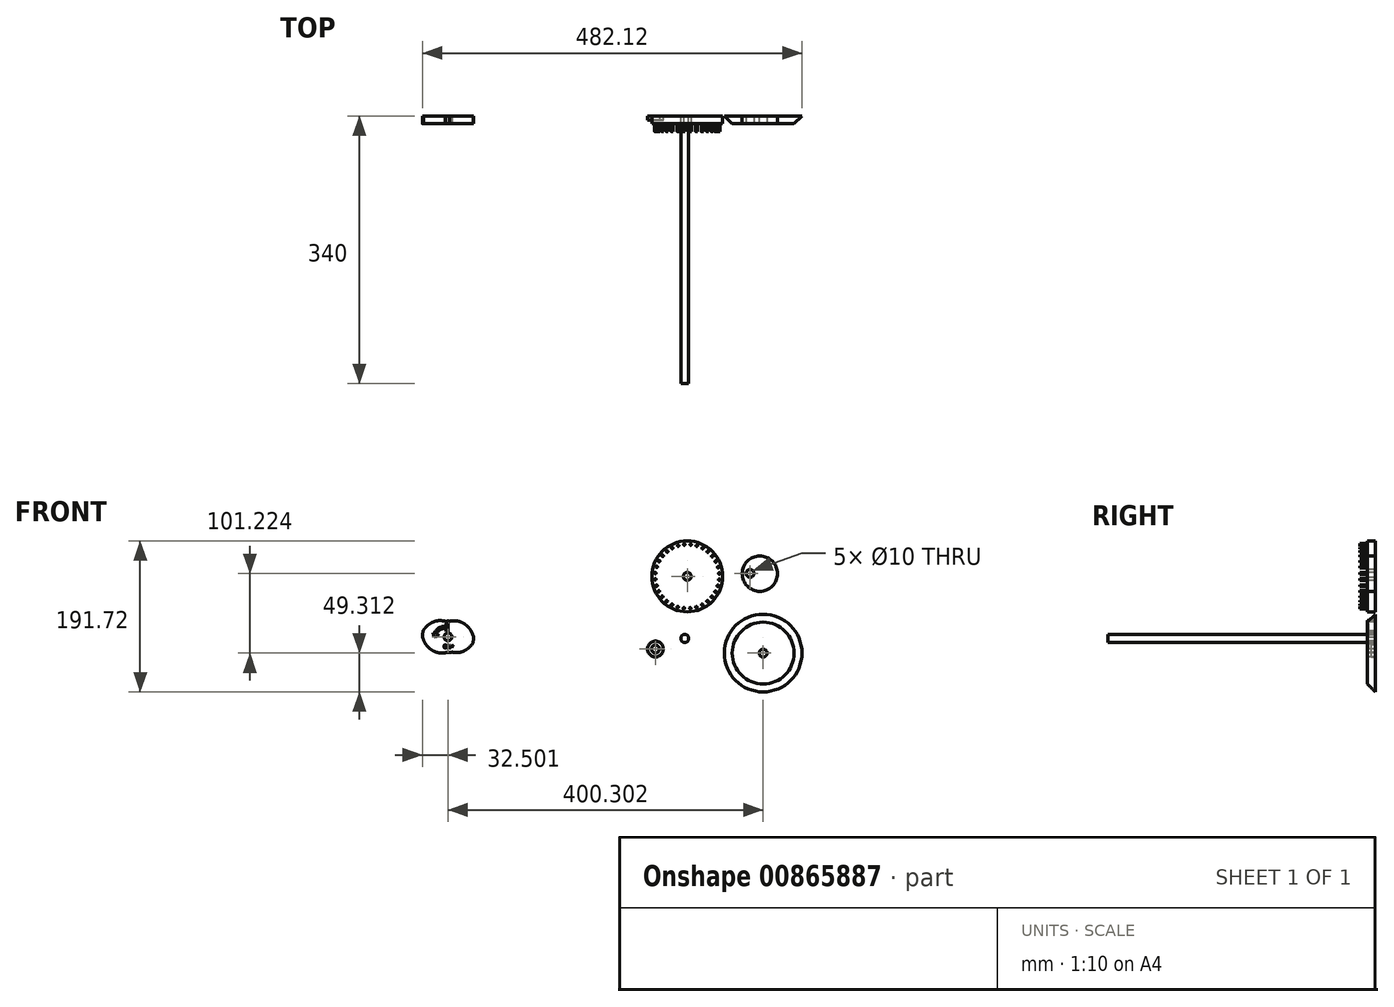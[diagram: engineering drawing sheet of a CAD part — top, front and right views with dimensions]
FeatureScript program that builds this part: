
annotation { "Feature Type Name" : "Feature", "Feature Type Description" : "" }
export const myFeature = defineFeature(function(context is Context, id is Id, definition is map)
    precondition{}
    {
        {
            var Q0;
            Q0=qCreatedBy(makeId("Front.planeOp"),FACE);
            var sketch = newSketch(context, id + "F0", { "sketchPlane" : qUnion([Q0])});
            skCircle(sketch, "E0", {"center": v(-46.7, 45.56) * mm, "radius": 45 * mm});
            skCircle(sketch, "E1", {"center": v(45.46, 49.07) * mm, "radius": 22.45 * mm});
            skCircle(sketch, "E2", {"center": v(49.66, -51.85) * mm, "radius": 49.31 * mm});
            skCircle(sketch, "E3", {"center": v(-350.64, -31.3) * mm, "radius": 20 * mm});
            skArc(sketch, "E4", {"start": v(-382.03, -22.88) * mm, "mid": v(-382.86, -27.05) * mm, "end": v(-383.14, -31.3) * mm});
            skLineSegment(sketch, "E5", {"start": v(-350.64, -11.3) * mm, "end": v(-350.64, 1.2) * mm});
            skLineSegment(sketch, "E6.1.0", {"start": v(-355.82, -11.98) * mm, "end": v(-359.05, 0.1) * mm});
            skLineSegment(sketch, "E6.2.0", {"start": v(-360.64, -13.97) * mm, "end": v(-366.89, -3.15) * mm});
            skLineSegment(sketch, "E6.3.0", {"start": v(-364.78, -17.15) * mm, "end": v(-373.62, -8.31) * mm});
            skLineSegment(sketch, "E6.4.0", {"start": v(-367.96, -21.3) * mm, "end": v(-378.79, -15.04) * mm});
            skLineSegment(sketch, "E6.5.0", {"start": v(-369.96, -26.12) * mm, "end": v(-382.03, -22.88) * mm});
            skLineSegment(sketch, "E6.6.0", {"start": v(-370.64, -31.3) * mm, "end": v(-383.14, -31.3) * mm});
            skLineSegment(sketch, "E6.7.0", {"start": v(-369.96, -36.47) * mm, "end": v(-382.03, -39.7) * mm});
            skLineSegment(sketch, "E6.8.0", {"start": v(-367.96, -41.3) * mm, "end": v(-378.79, -47.54) * mm});
            skLineSegment(sketch, "E6.9.0", {"start": v(-364.78, -45.44) * mm, "end": v(-373.62, -54.27) * mm});
            skLineSegment(sketch, "E6.10.0", {"start": v(-360.64, -48.61) * mm, "end": v(-366.89, -59.44) * mm});
            skLineSegment(sketch, "E6.11.0", {"start": v(-355.82, -50.61) * mm, "end": v(-359.05, -62.69) * mm});
            skLineSegment(sketch, "E6.12.0", {"start": v(-350.64, -51.3) * mm, "end": v(-350.64, -63.8) * mm});
            skLineSegment(sketch, "E6.13.0", {"start": v(-345.46, -50.61) * mm, "end": v(-342.23, -62.69) * mm});
            skLineSegment(sketch, "E6.14.0", {"start": v(-340.64, -48.61) * mm, "end": v(-334.39, -59.44) * mm});
            skLineSegment(sketch, "E6.15.0", {"start": v(-336.5, -45.44) * mm, "end": v(-327.66, -54.27) * mm});
            skLineSegment(sketch, "E6.16.0", {"start": v(-333.32, -41.3) * mm, "end": v(-322.5, -47.54) * mm});
            skLineSegment(sketch, "E6.17.0", {"start": v(-331.32, -36.47) * mm, "end": v(-319.25, -39.7) * mm});
            skLineSegment(sketch, "E6.18.0", {"start": v(-330.64, -31.3) * mm, "end": v(-318.14, -31.3) * mm});
            skLineSegment(sketch, "E6.19.0", {"start": v(-331.32, -26.12) * mm, "end": v(-319.25, -22.88) * mm});
            skLineSegment(sketch, "E6.20.0", {"start": v(-333.32, -21.3) * mm, "end": v(-322.5, -15.04) * mm});
            skLineSegment(sketch, "E6.21.0", {"start": v(-336.5, -17.15) * mm, "end": v(-327.66, -8.31) * mm});
            skLineSegment(sketch, "E6.22.0", {"start": v(-340.64, -13.97) * mm, "end": v(-334.39, -3.15) * mm});
            skLineSegment(sketch, "E6.23.0", {"start": v(-345.46, -11.98) * mm, "end": v(-342.23, 0.1) * mm});
            skPoint(sketch, "E7", {"position": v(-382.03, -22.88) * mm});
            skPoint(sketch, "E8", {"position": v(-383.14, -31.3) * mm});
            skPoint(sketch, "E9", {"position": v(-318.14, -31.3) * mm});
            skPoint(sketch, "E10", {"position": v(-319.25, -39.7) * mm});
            skPoint(sketch, "E11", {"position": v(-353.64, -11.52) * mm});
            skPoint(sketch, "E12", {"position": v(-345.46, -50.61) * mm});
            skPoint(sketch, "E13", {"position": v(-352.64, -51.2) * mm});
            skLineSegment(sketch, "E14", {"start": v(-350.64, -31.3) * mm, "end": v(-345.46, -50.61) * mm, "construction": true});
            skLineSegment(sketch, "E15", {"start": v(-350.64, -31.3) * mm, "end": v(-352.64, -51.2) * mm, "construction": true});
            skLineSegment(sketch, "E16", {"start": v(-350.64, -31.3) * mm, "end": v(-353.64, -11.52) * mm, "construction": true});
            skLineSegment(sketch, "E17", {"start": v(-350.64, -31.3) * mm, "end": v(-348.64, -11.4) * mm, "construction": true});
            skPoint(sketch, "E18", {"position": v(-348.64, -11.4) * mm});
            skPoint(sketch, "E19", {"position": v(-345.2, -11) * mm});
            skPoint(sketch, "E20", {"position": v(-338.99, -11.12) * mm});
            skPoint(sketch, "E21", {"position": v(-332.54, -13.2) * mm});
            skPoint(sketch, "E22", {"position": v(-326.48, -17.34) * mm});
            skPoint(sketch, "E23", {"position": v(-321.47, -23.48) * mm});
            skPoint(sketch, "E24", {"position": v(-325.2, -45.98) * mm});
            skPoint(sketch, "E25", {"position": v(-332.08, -49.86) * mm});
            skPoint(sketch, "E26", {"position": v(-339.08, -51.32) * mm});
            skPoint(sketch, "E27", {"position": v(-356.07, -51.58) * mm});
            skPoint(sketch, "E28", {"position": v(-362.29, -51.47) * mm});
            skPoint(sketch, "E29", {"position": v(-368.74, -49.4) * mm});
            skPoint(sketch, "E30", {"position": v(-374.8, -45.24) * mm});
            skPoint(sketch, "E31", {"position": v(-379.81, -39.11) * mm});
            skPoint(sketch, "E32", {"position": v(-376.3, -16.48) * mm});
            skPoint(sketch, "E33", {"position": v(-369.55, -12.38) * mm});
            skPoint(sketch, "E34", {"position": v(-362.57, -10.62) * mm});
            skPoint(sketch, "E35", {"position": v(-356.07, -11) * mm});
            skFitSpline(sketch, "E36", {"points": [v(-382.03, -22.88) * mm, v(-376.3, -16.48) * mm, v(-369.55, -12.38) * mm, v(-362.57, -10.62) * mm, v(-356.07, -11) * mm, v(-353.64, -11.52) * mm], "startDerivative": vector(23.19, 29.3) * mm, "endDerivative": vector(16.8, -4.09) * mm});
            skFitSpline(sketch, "E37", {"points": [v(-348.64, -11.4) * mm, v(-345.2, -11) * mm, v(-338.99, -11.12) * mm, v(-332.54, -13.2) * mm, v(-326.48, -17.34) * mm, v(-321.47, -23.48) * mm, v(-318.14, -31.3) * mm], "startDerivative": vector(26.16, 3.52) * mm, "endDerivative": vector(15.37, -42.82) * mm});
            skFitSpline(sketch, "E38", {"points": [v(-319.25, -39.7) * mm, v(-325.2, -45.98) * mm, v(-332.08, -49.86) * mm, v(-339.08, -51.32) * mm, v(-345.46, -50.61) * mm], "startDerivative": vector(-21.1, -25.12) * mm, "endDerivative": vector(-27.27, 4.92) * mm});
            skFitSpline(sketch, "E39", {"points": [v(-352.64, -51.2) * mm, v(-356.07, -51.58) * mm, v(-362.29, -51.47) * mm, v(-368.74, -49.4) * mm, v(-374.8, -45.24) * mm, v(-379.81, -39.11) * mm, v(-383.14, -31.3) * mm], "startDerivative": vector(-26.17, -3.52) * mm, "endDerivative": vector(-15.37, 42.82) * mm});
            skArc(sketch, "E40.trimOffspring", {"start": v(-319.25, -39.7) * mm, "mid": v(-318.42, -35.54) * mm, "end": v(-318.14, -31.3) * mm});
            skSolve(sketch);
        }
        {
            var Q0;
            Q0=qSketchRegion(id+"F0",true);
            extrude(context, id + "F1", {"entities" : qUnion([Q0]), "depth" : 10 * mm, "offsetDistance" : 25 * mm});
        }
        {
            var Q0;
            Q0=makeQuery(id+"F1.opExtrude","CAP_FACE",FACE,{"disambiguationData":[OSD([sQuery(id+"F0.wireOp",EDGE,"E0")])],"isStart":false});
            var sketch = newSketch(context, id + "F2", { "sketchPlane" : qUnion([Q0])});
            skCircle(sketch, "E41", {"center": v(-46.7, 45.56) * mm, "radius": 5 * mm});
            skSolve(sketch);
        }
        {
            var Q0;
            Q0=qSketchRegion(id+"F2",true);
            extrude(context, id + "F3", {"entities" : qUnion([Q0]), "operationType" : NewBodyOperationType.REMOVE, "endBound" : BoundingType.THROUGH_ALL, "oppositeDirection" : true, "depth" : 25 * mm, "offsetDistance" : 25 * mm});
        }
        {
            var Q0;
            Q0=makeQuery(id+"F1.opExtrude","CAP_FACE",FACE,{"disambiguationData":[OSD([sQuery(id+"F0.wireOp",EDGE,"E2")])],"isStart":false});
            var sketch = newSketch(context, id + "F4", { "sketchPlane" : qUnion([Q0])});
            skCircle(sketch, "E42", {"center": v(49.66, -51.85) * mm, "radius": 5 * mm});
            skSolve(sketch);
        }
        {
            var Q0;
            Q0=qSketchRegion(id+"F4",true);
            extrude(context, id + "F5", {"entities" : qUnion([Q0]), "operationType" : NewBodyOperationType.REMOVE, "endBound" : BoundingType.THROUGH_ALL, "oppositeDirection" : true, "depth" : 25 * mm, "offsetDistance" : 25 * mm});
        }
        {
            var Q0;
            Q0=makeQuery(id+"F1.opExtrude","CAP_FACE",FACE,{"disambiguationData":[OSD([sQuery(id+"F0.wireOp",EDGE,"E1")])],"isStart":false});
            var sketch = newSketch(context, id + "F6", { "sketchPlane" : qUnion([Q0])});
            skCircle(sketch, "E43", {"center": v(33.01, 49.38) * mm, "radius": 5 * mm});
            skSolve(sketch);
        }
        {
            var Q0;
            Q0=qSketchRegion(id+"F6",true);
            extrude(context, id + "F7", {"entities" : qUnion([Q0]), "operationType" : NewBodyOperationType.REMOVE, "endBound" : BoundingType.THROUGH_ALL, "oppositeDirection" : true, "depth" : 25 * mm, "offsetDistance" : 25 * mm});
        }
        {
            var Q0;
            Q0=makeQuery(id+"F1.opExtrude","CAP_EDGE",EDGE,{"disambiguationData":[OSD([sQuery(id+"F0.wireOp",EDGE,"E2")])],"isStart":false});
            chamfer(context, id + "F8", {"entities" : qUnion([Q0]), "width" : 10 * mm, "tangentPropagation" : true});
        }
        {
            var Q0;
            Q0=qCreatedBy(makeId("Front.planeOp"),FACE);
            var sketch = newSketch(context, id + "F9", { "sketchPlane" : qUnion([Q0])});
            skCircle(sketch, "E44", {"center": v(-49.88, -33.26) * mm, "radius": 5 * mm});
            skSolve(sketch);
        }
        {
            var Q0;
            Q0=qSketchRegion(id+"F9",true);
            extrude(context, id + "F10", {"entities" : qUnion([Q0]), "depth" : 340 * mm, "offsetDistance" : 25 * mm});
        }
        {
            var Q0;
            Q0=qCreatedBy(makeId("Front.planeOp"),FACE);
            var sketch = newSketch(context, id + "F11", { "sketchPlane" : qUnion([Q0])});
            skCircle(sketch, "E45", {"center": v(-87.17, -46.68) * mm, "radius": 10 * mm});
            skSolve(sketch);
        }
        {
            var Q0;
            Q0=qSketchRegion(id+"F11",true);
            extrude(context, id + "F12", {"entities" : qUnion([Q0]), "depth" : 5 * mm, "offsetDistance" : 25 * mm});
        }
        {
            var Q0;
            Q0=makeQuery(id+"F12.opExtrude","CAP_FACE",FACE,{"disambiguationData":[OSD([sQuery(id+"F11.wireOp",EDGE,"E45")])],"isStart":false});
            var sketch = newSketch(context, id + "F13", { "sketchPlane" : qUnion([Q0])});
            skCircle(sketch, "E46", {"center": v(-87.17, -46.68) * mm, "radius": 5 * mm});
            skSolve(sketch);
        }
        {
            var Q0;
            Q0=qSketchRegion(id+"F13",true);
            extrude(context, id + "F14", {"entities" : qUnion([Q0]), "operationType" : NewBodyOperationType.REMOVE, "endBound" : BoundingType.THROUGH_ALL, "oppositeDirection" : true, "depth" : 25 * mm, "offsetDistance" : 25 * mm});
        }
        {
            var Q0;
            Q0=makeQuery(id+"F1.opExtrude","CAP_FACE",FACE,{"disambiguationData":[OSD([sQuery(id+"F0.wireOp",EDGE,"E0")])],"isStart":false});
            var sketch = newSketch(context, id + "F15", { "sketchPlane" : qUnion([Q0])});
            skArc(sketch, "E47.cCircle", {"start": v(-41.46, 85.98) * mm, "mid": v(-54.9, 5.65) * mm, "end": v(-35.59, 84.77) * mm, "construction": true});
            skLineSegment(sketch, "E47.0", {"start": v(-21.04, 13.9) * mm, "end": v(-27.7, 9.5) * mm});
            skLineSegment(sketch, "E47.1", {"start": v(-27.7, 9.5) * mm, "end": v(-35.1, 6.5) * mm});
            skLineSegment(sketch, "E47.2", {"start": v(-35.1, 6.5) * mm, "end": v(-42.95, 4.99) * mm});
            skLineSegment(sketch, "E47.3", {"start": v(-42.95, 4.99) * mm, "end": v(-50.94, 5.03) * mm});
            skLineSegment(sketch, "E47.4", {"start": v(-50.94, 5.03) * mm, "end": v(-58.76, 6.64) * mm});
            skLineSegment(sketch, "E47.5", {"start": v(-58.76, 6.64) * mm, "end": v(-66.13, 9.74) * mm});
            skLineSegment(sketch, "E47.6", {"start": v(-66.13, 9.74) * mm, "end": v(-72.74, 14.22) * mm});
            skLineSegment(sketch, "E47.7", {"start": v(-72.74, 14.22) * mm, "end": v(-78.35, 19.9) * mm});
            skLineSegment(sketch, "E47.8", {"start": v(-78.35, 19.9) * mm, "end": v(-82.75, 26.57) * mm});
            skLineSegment(sketch, "E47.9", {"start": v(-82.75, 26.57) * mm, "end": v(-85.76, 33.97) * mm});
            skLineSegment(sketch, "E47.10", {"start": v(-85.76, 33.97) * mm, "end": v(-87.27, 41.82) * mm});
            skLineSegment(sketch, "E47.11", {"start": v(-87.27, 41.82) * mm, "end": v(-87.23, 49.8) * mm});
            skLineSegment(sketch, "E47.12", {"start": v(-87.23, 49.8) * mm, "end": v(-85.62, 57.63) * mm});
            skLineSegment(sketch, "E47.13", {"start": v(-85.62, 57.63) * mm, "end": v(-82.52, 65) * mm});
            skLineSegment(sketch, "E47.14", {"start": v(-82.52, 65) * mm, "end": v(-78.04, 71.6) * mm});
            skLineSegment(sketch, "E47.15", {"start": v(-78.04, 71.6) * mm, "end": v(-72.36, 77.22) * mm});
            skLineSegment(sketch, "E47.16", {"start": v(-72.36, 77.22) * mm, "end": v(-65.69, 81.62) * mm});
            skLineSegment(sketch, "E47.17", {"start": v(-65.69, 81.62) * mm, "end": v(-58.29, 84.63) * mm});
            skLineSegment(sketch, "E47.18", {"start": v(-58.29, 84.63) * mm, "end": v(-50.44, 86.14) * mm});
            skLineSegment(sketch, "E47.19", {"start": v(-50.44, 86.14) * mm, "end": v(-42.46, 86.1) * mm});
            skLineSegment(sketch, "E47.20", {"start": v(-42.46, 86.1) * mm, "end": v(-41.48, 85.9) * mm});
            skLineSegment(sketch, "E47.21", {"start": v(-34.63, 84.49) * mm, "end": v(-27.27, 81.38) * mm});
            skLineSegment(sketch, "E47.22", {"start": v(-27.27, 81.38) * mm, "end": v(-20.65, 76.9) * mm});
            skLineSegment(sketch, "E47.23", {"start": v(-20.65, 76.9) * mm, "end": v(-15.04, 71.22) * mm});
            skLineSegment(sketch, "E47.24", {"start": v(-15.04, 71.22) * mm, "end": v(-10.64, 64.55) * mm});
            skLineSegment(sketch, "E47.25", {"start": v(-10.64, 64.55) * mm, "end": v(-7.63, 57.15) * mm});
            skLineSegment(sketch, "E47.26", {"start": v(-7.63, 57.15) * mm, "end": v(-6.12, 49.31) * mm});
            skLineSegment(sketch, "E47.27", {"start": v(-6.12, 49.31) * mm, "end": v(-6.17, 41.32) * mm});
            skLineSegment(sketch, "E47.28", {"start": v(-6.17, 41.32) * mm, "end": v(-7.77, 33.5) * mm});
            skLineSegment(sketch, "E47.29", {"start": v(-7.77, 33.5) * mm, "end": v(-10.88, 26.14) * mm});
            skLineSegment(sketch, "E47.30", {"start": v(-10.88, 26.14) * mm, "end": v(-15.36, 19.52) * mm});
            skLineSegment(sketch, "E47.31", {"start": v(-15.36, 19.52) * mm, "end": v(-21.04, 13.9) * mm});
            skCircle(sketch, "E48", {"center": v(-15.04, 71.22) * mm, "radius": 1 * mm});
            skCircle(sketch, "E49", {"center": v(-10.64, 64.55) * mm, "radius": 1 * mm});
            skCircle(sketch, "E50", {"center": v(-7.63, 57.15) * mm, "radius": 1 * mm});
            skCircle(sketch, "E51", {"center": v(-6.12, 49.31) * mm, "radius": 1 * mm});
            skCircle(sketch, "E52", {"center": v(-6.17, 41.32) * mm, "radius": 1 * mm});
            skCircle(sketch, "E53", {"center": v(-7.77, 33.5) * mm, "radius": 1 * mm});
            skCircle(sketch, "E54", {"center": v(-10.88, 26.14) * mm, "radius": 1 * mm});
            skCircle(sketch, "E55", {"center": v(-15.36, 19.52) * mm, "radius": 1 * mm});
            skCircle(sketch, "E56", {"center": v(-21.04, 13.9) * mm, "radius": 1 * mm});
            skCircle(sketch, "E57", {"center": v(-27.7, 9.5) * mm, "radius": 1 * mm});
            skCircle(sketch, "E58", {"center": v(-35.1, 6.5) * mm, "radius": 1 * mm});
            skCircle(sketch, "E59", {"center": v(-42.95, 4.99) * mm, "radius": 1 * mm});
            skCircle(sketch, "E60", {"center": v(-50.94, 5.03) * mm, "radius": 1 * mm});
            skCircle(sketch, "E61", {"center": v(-58.76, 6.64) * mm, "radius": 1 * mm});
            skCircle(sketch, "E62", {"center": v(-66.13, 9.74) * mm, "radius": 1 * mm});
            skCircle(sketch, "E63", {"center": v(-72.74, 14.22) * mm, "radius": 1 * mm});
            skCircle(sketch, "E64", {"center": v(-78.35, 19.9) * mm, "radius": 1 * mm});
            skCircle(sketch, "E65", {"center": v(-87.27, 41.82) * mm, "radius": 1 * mm});
            skCircle(sketch, "E66", {"center": v(-85.76, 33.97) * mm, "radius": 1 * mm});
            skCircle(sketch, "E67", {"center": v(-82.75, 26.57) * mm, "radius": 1 * mm});
            skCircle(sketch, "E68", {"center": v(-87.23, 49.8) * mm, "radius": 1 * mm});
            skCircle(sketch, "E69", {"center": v(-85.62, 57.63) * mm, "radius": 1 * mm});
            skCircle(sketch, "E70", {"center": v(-82.52, 65) * mm, "radius": 1 * mm});
            skCircle(sketch, "E71", {"center": v(-78.04, 71.6) * mm, "radius": 1 * mm});
            skCircle(sketch, "E72", {"center": v(-72.36, 77.22) * mm, "radius": 1 * mm});
            skCircle(sketch, "E73", {"center": v(-65.69, 81.62) * mm, "radius": 1 * mm});
            skCircle(sketch, "E74", {"center": v(-58.29, 84.63) * mm, "radius": 1 * mm});
            skCircle(sketch, "E75", {"center": v(-50.44, 86.14) * mm, "radius": 1 * mm});
            skCircle(sketch, "E76", {"center": v(-42.46, 86.1) * mm, "radius": 1 * mm});
            skCircle(sketch, "E77", {"center": v(-34.63, 84.49) * mm, "radius": 1 * mm});
            skCircle(sketch, "E78", {"center": v(-27.27, 81.38) * mm, "radius": 1 * mm});
            skCircle(sketch, "E79", {"center": v(-20.65, 76.9) * mm, "radius": 1 * mm});
            skLineSegment(sketch, "E80.trimOffspring", {"start": v(-35.61, 84.69) * mm, "end": v(-34.63, 84.49) * mm});
            skSolve(sketch);
        }
        {
            var Q0;
            Q0=qSketchRegion(id+"F15",true);
            extrude(context, id + "F16", {"entities" : qUnion([Q0]), "operationType" : NewBodyOperationType.ADD, "depth" : 10 * mm, "offsetDistance" : 25 * mm});
        }
        {
            var Q0;
            Q0=makeQuery(id+"F1.opExtrude","CAP_FACE",FACE,{"disambiguationData":[OSD([sQuery(id+"F0.wireOp",EDGE,"E3"),sQuery(id+"F0.wireOp",EDGE,"E4"),sQuery(id+"F0.wireOp",EDGE,"E36"),sQuery(id+"F0.wireOp",EDGE,"E37"),sQuery(id+"F0.wireOp",EDGE,"E38"),sQuery(id+"F0.wireOp",EDGE,"E39"),sQuery(id+"F0.wireOp",EDGE,"E40.trimOffspring")])],"isStart":false});
            var sketch = newSketch(context, id + "F17", { "sketchPlane" : qUnion([Q0])});
            skCircle(sketch, "E81", {"center": v(-350.64, -31.3) * mm, "radius": 5 * mm});
            skSolve(sketch);
        }
        {
            var Q0;
            Q0 = qSketchRegion(id + "F17", true);
            extrude(context, id + "F18", {"entities" : qUnion([Q0]), "operationType" : NewBodyOperationType.REMOVE, "oppositeDirection" : true, "depth" : 25 * mm, "offsetDistance" : 25 * mm});
        }
        {
            var Q0;
            Q0=makeQuery(id+"F1.opExtrude","CAP_FACE",FACE,{"disambiguationData":[OSD([sQuery(id+"F0.wireOp",EDGE,"E3"),sQuery(id+"F0.wireOp",EDGE,"E4"),sQuery(id+"F0.wireOp",EDGE,"E36"),sQuery(id+"F0.wireOp",EDGE,"E37"),sQuery(id+"F0.wireOp",EDGE,"E38"),sQuery(id+"F0.wireOp",EDGE,"E39"),sQuery(id+"F0.wireOp",EDGE,"E40.trimOffspring")])],"isStart":false});
            var sketch = newSketch(context, id + "F19", { "sketchPlane" : qUnion([Q0])});
            skLineSegment(sketch, "E82", {"start": v(-350.7, -14.28) * mm, "end": v(-350.7, -24.2) * mm});
            skLineSegment(sketch, "E83", {"start": v(-350.7, -24.2) * mm, "end": v(-352.94, -24.2) * mm});
            skLineSegment(sketch, "E84", {"start": v(-352.94, -24.2) * mm, "end": v(-352.94, -20.48) * mm});
            skArc(sketch, "E85", {"start": v(-352.94, -20.48) * mm, "mid": v(-360.46, -22.08) * mm, "end": v(-365.35, -28) * mm});
            skLineSegment(sketch, "E86", {"start": v(-350.7, -14.28) * mm, "end": v(-353.02, -14.28) * mm});
            skLineSegment(sketch, "E87", {"start": v(-353.02, -14.28) * mm, "end": v(-353.02, -17.92) * mm});
            skArc(sketch, "E88", {"start": v(-353.02, -17.92) * mm, "mid": v(-361.68, -19.58) * mm, "end": v(-367.42, -26.27) * mm});
            skLineSegment(sketch, "E89", {"start": v(-367.42, -26.27) * mm, "end": v(-369.65, -25.36) * mm});
            skLineSegment(sketch, "E90", {"start": v(-369.65, -25.36) * mm, "end": v(-368.4, -31.32) * mm});
            skLineSegment(sketch, "E91", {"start": v(-368.4, -31.32) * mm, "end": v(-361.95, -29.97) * mm});
            skLineSegment(sketch, "E92", {"start": v(-361.95, -29.97) * mm, "end": v(-365.35, -28) * mm});
            skText(sketch, "E93", { "text": "Cour", "fontName": "OpenSans-Regular.ttf"});
            const initialGuessF19  = {"E93": [-0.35625, -0.0453, 1, 0, 0.00389]};
            skSetInitialGuess(sketch, initialGuessF19);
            skSolve(sketch);
        }
        {
            var Q0;
            Q0 = qSketchRegion(id + "F19", true);
            extrude(context, id + "F20", {"entities" : qUnion([Q0]), "operationType" : NewBodyOperationType.REMOVE, "oppositeDirection" : true, "depth" : 1 * mm, "offsetDistance" : 25 * mm});
        }
    });
